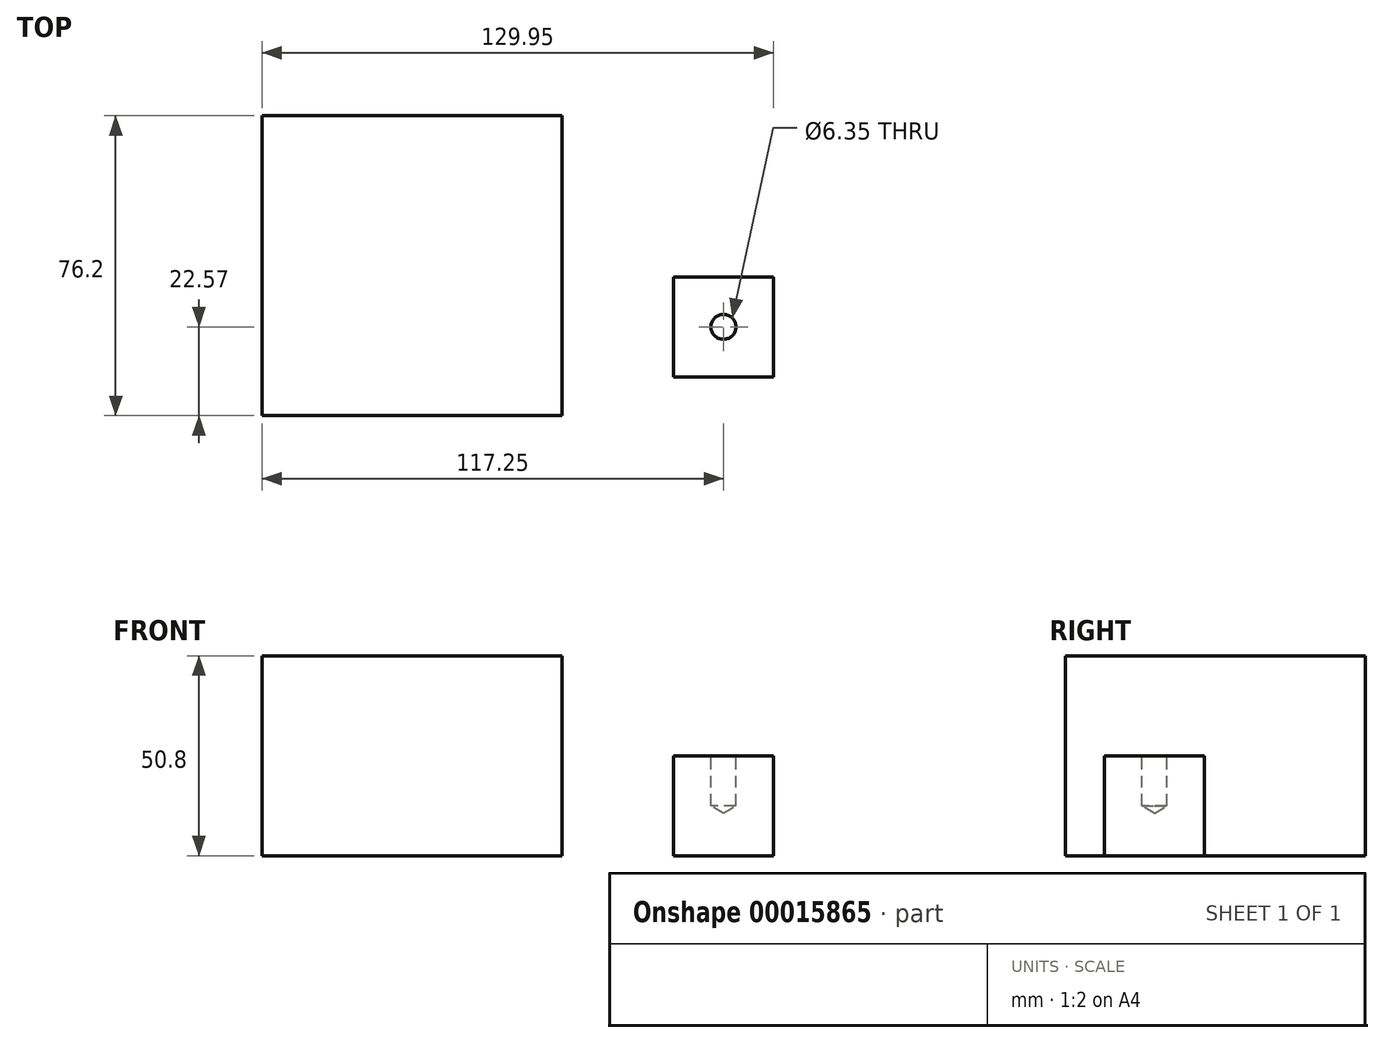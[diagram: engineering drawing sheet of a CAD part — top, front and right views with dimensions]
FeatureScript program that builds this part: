
annotation { "Feature Type Name" : "Feature", "Feature Type Description" : "" }
export const myFeature = defineFeature(function(context is Context, id is Id, definition is map)
    precondition{}
    {
        {
            var Q0;
            Q0=qCreatedBy(makeId("Top.planeOp"),FACE);
            var sketch = newSketch(context, id + "F0", { "sketchPlane" : qUnion([Q0])});
            skLineSegment(sketch, "E0.bottom", {"start": v(0, 0) * mm, "end": v(25.4, 0) * mm});
            skLineSegment(sketch, "E0.top", {"start": v(0, 25.4) * mm, "end": v(25.4, 25.4) * mm});
            skLineSegment(sketch, "E0.left", {"start": v(0, 0) * mm, "end": v(0, 25.4) * mm});
            skLineSegment(sketch, "E0.right", {"start": v(25.4, 0) * mm, "end": v(25.4, 25.4) * mm});
            skSolve(sketch);
        }
        {
            var Q0;
            Q0 = qSketchRegion(id + "F0", true);
            extrude(context, id + "F1", {"entities" : qUnion([Q0]), "depth" : 25.4 * mm});
        }
        {
            var Q0;
            Q0=makeQuery(id+"F1.opExtrude","CAP_FACE",FACE,{"disambiguationData":[OSD([sQuery(id+"F0.wireOp",EDGE,"E0.bottom"),sQuery(id+"F0.wireOp",EDGE,"E0.top"),sQuery(id+"F0.wireOp",EDGE,"E0.left"),sQuery(id+"F0.wireOp",EDGE,"E0.right")])],"isStart":false});
            var sketch = newSketch(context, id + "F2", { "sketchPlane" : qUnion([Q0])});
            skCircle(sketch, "E1", {"center": v(12.7, 12.7) * mm, "radius": 3.18 * mm});
            skSolve(sketch);
        }
        {
            var Q0;
            Q0=sQuery(id+"F2.wireOp",VERTEX,"E1.center");
            var Q1;
            Q1=makeQuery(id+"F1.opExtrude","SWEPT_BODY",BODY,{"disambiguationData":[OSD([sQuery(id+"F0.wireOp",EDGE,"E0.bottom"),sQuery(id+"F0.wireOp",EDGE,"E0.top"),sQuery(id+"F0.wireOp",EDGE,"E0.left"),sQuery(id+"F0.wireOp",EDGE,"E0.right")])]});
            hole(context, id + "F3", {"style" : HoleStyle.SIMPLE, "holeDiameter" : 6.35 * mm, "endStyle" : HoleEndStyle.BLIND, "holeDepth" : 12.7 * mm, "locations" : qUnion([Q0]), "scope" : qUnion([Q1])});
        }
        {
            var Q0;
            Q0=qCreatedBy(makeId("Top.planeOp"),FACE);
            var sketch = newSketch(context, id + "F4", { "sketchPlane" : qUnion([Q0])});
            skLineSegment(sketch, "E2.bottom", {"start": v(-104.55, 66.33) * mm, "end": v(-28.35, 66.33) * mm});
            skLineSegment(sketch, "E2.top", {"start": v(-104.55, -9.87) * mm, "end": v(-28.35, -9.87) * mm});
            skLineSegment(sketch, "E2.left", {"start": v(-104.55, 66.33) * mm, "end": v(-104.55, -9.87) * mm});
            skLineSegment(sketch, "E2.right", {"start": v(-28.35, 66.33) * mm, "end": v(-28.35, -9.87) * mm});
            skSolve(sketch);
        }
        {
            var Q0;
            Q0=makeQuery(id+"F4.imprint","IMPRINT",FACE,{"disambiguationData":[TD([[makeQuery(id+"F4.imprint","IMPRINT",EDGE,{"derivedFrom":sQuery(id+"F4.wireOp",EDGE,"E2.bottom")}),-1.0]])]});
            extrude(context, id + "F5", {"entities" : qUnion([Q0]), "depth" : 50.8 * mm});
        }
    });
